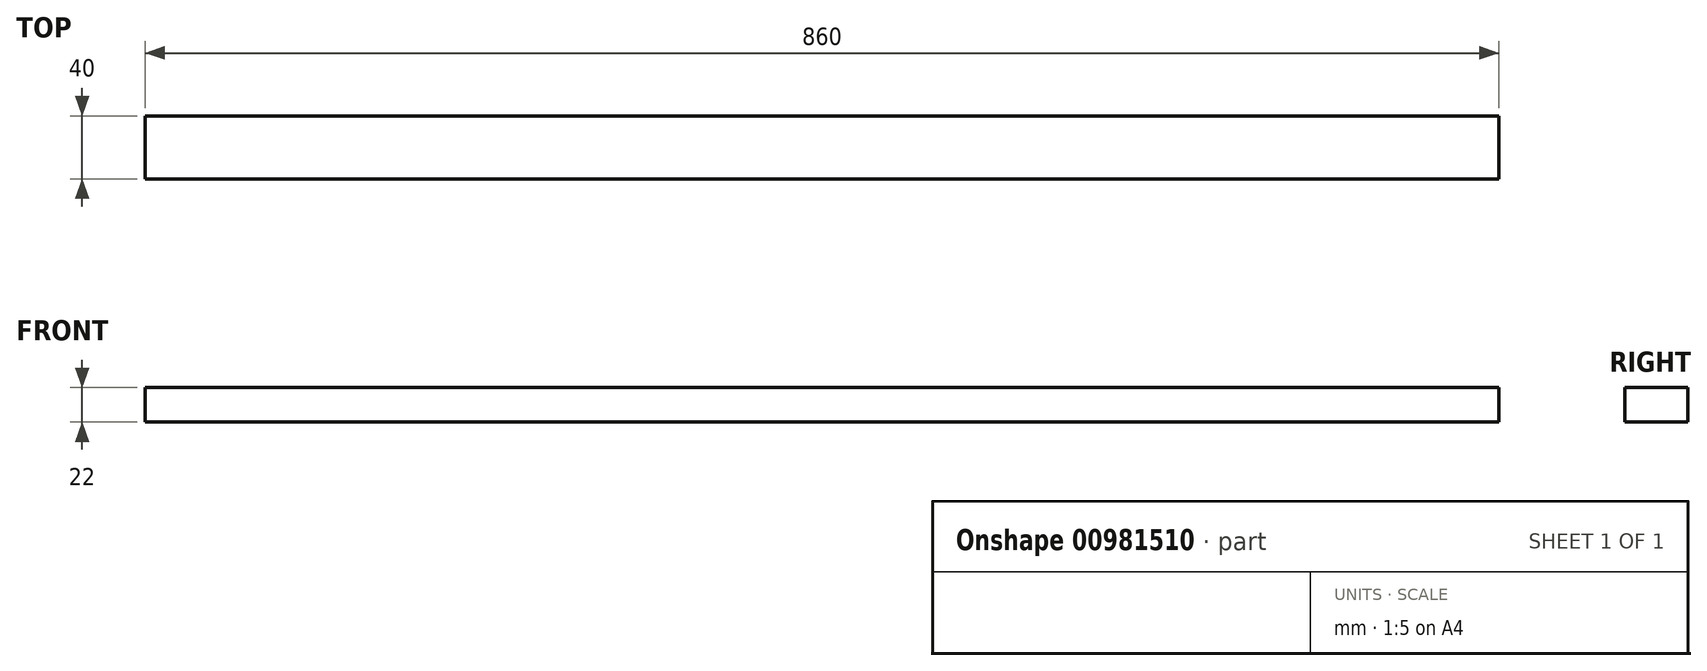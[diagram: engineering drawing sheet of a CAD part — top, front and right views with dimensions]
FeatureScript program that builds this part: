
annotation { "Feature Type Name" : "Feature", "Feature Type Description" : "" }
export const myFeature = defineFeature(function(context is Context, id is Id, definition is map)
    precondition{}
    {
        {
            var Q0;
            Q0=qCreatedBy(makeId("Right.planeOp"),FACE);
            var sketch = newSketch(context, id + "F0", { "sketchPlane" : qUnion([Q0])});
            skLineSegment(sketch, "E0.bottom", {"start": v(-30.65, 49.88) * mm, "end": v(9.35, 49.88) * mm});
            skLineSegment(sketch, "E0.top", {"start": v(-30.65, 27.88) * mm, "end": v(9.35, 27.88) * mm});
            skLineSegment(sketch, "E0.left", {"start": v(-30.65, 49.88) * mm, "end": v(-30.65, 27.88) * mm});
            skLineSegment(sketch, "E0.right", {"start": v(9.35, 49.88) * mm, "end": v(9.35, 27.88) * mm});
            skLineSegment(sketch, "E1.bottom", {"start": v(-30.65, 45.88) * mm, "end": v(-20.65, 45.88) * mm});
            skLineSegment(sketch, "E1.top", {"start": v(-30.65, 37.88) * mm, "end": v(-20.65, 37.88) * mm});
            skLineSegment(sketch, "E1.left", {"start": v(-30.65, 45.88) * mm, "end": v(-30.65, 37.88) * mm});
            skLineSegment(sketch, "E1.right", {"start": v(-20.65, 45.88) * mm, "end": v(-20.65, 37.88) * mm});
            skSolve(sketch);
        }
        {
            var Q0;
            Q0=makeQuery(id+"F0.imprint","IMPRINT",FACE,{"disambiguationData":[TD([[makeQuery(id+"F0.imprint","IMPRINT",EDGE,{"derivedFrom":sQuery(id+"F0.wireOp",EDGE,"E1.bottom")}),-1.0]])]});
            var Q1;
            {var subQ4=sQuery(id+"F0.wireOp",EDGE,"E0.bottom");Q1=makeQuery(id+"F0.imprint","IMPRINT",FACE,{"disambiguationData":[TD([[makeQuery(id+"F0.imprint","IMPRINT",EDGE,{"derivedFrom":subQ4}),-1.0]])]});}
            extrude(context, id + "F1", {"entities" : qUnion([Q0, Q1]), "depth" : 860 * mm, "offsetDistance" : 25 * mm});
        }
    });
